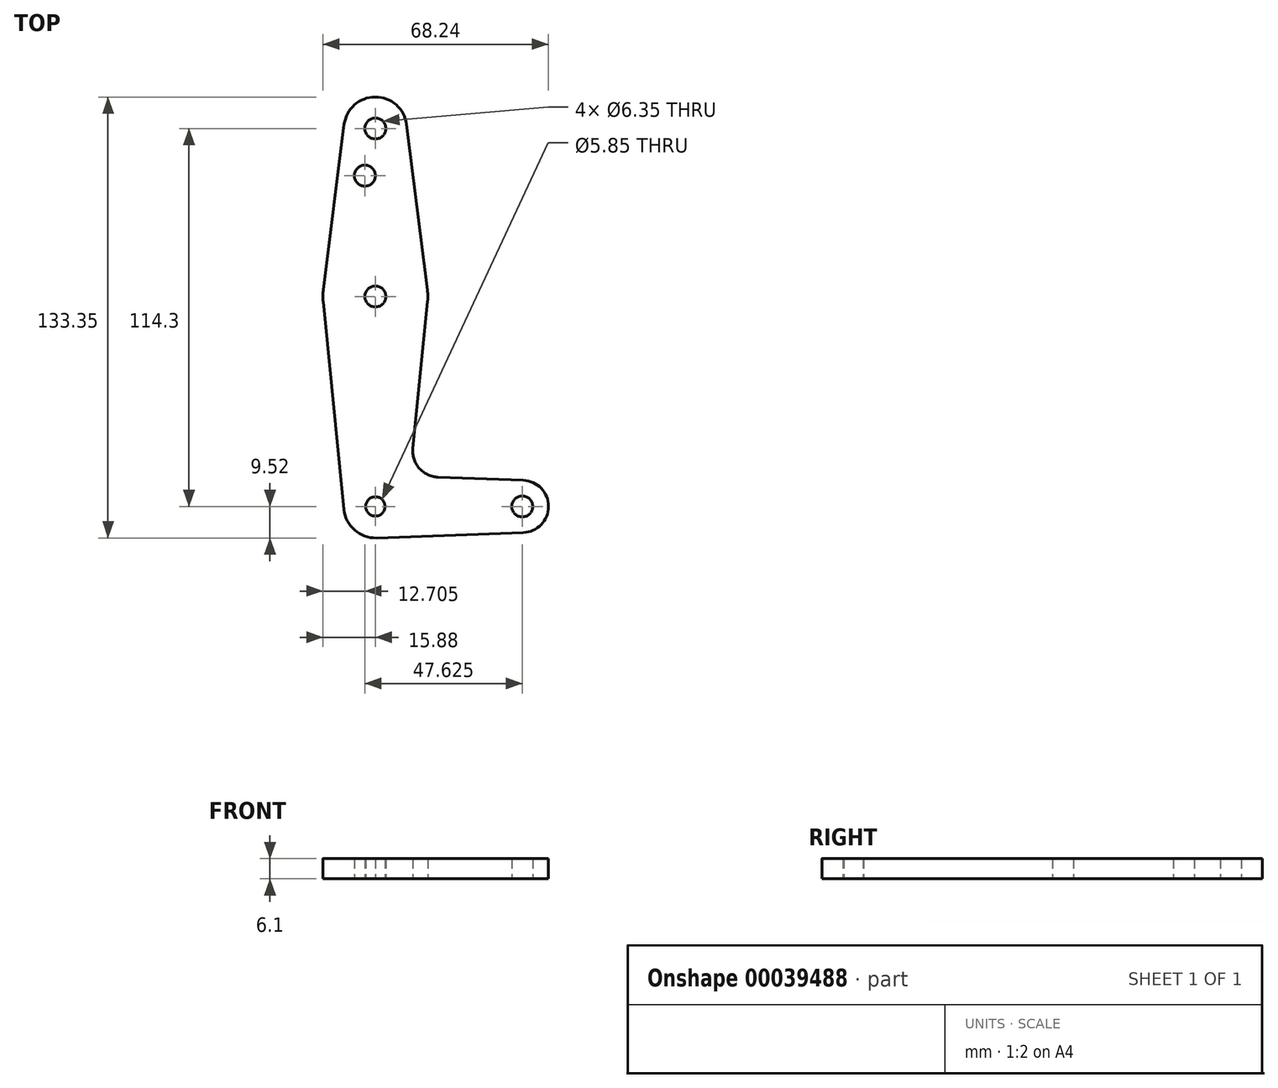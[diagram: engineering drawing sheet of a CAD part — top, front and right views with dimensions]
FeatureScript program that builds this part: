
annotation { "Feature Type Name" : "Feature", "Feature Type Description" : "" }
export const myFeature = defineFeature(function(context is Context, id is Id, definition is map)
    precondition{}
    {
        {
            var Q0;
            Q0=qCreatedBy(makeId("Top.planeOp"),FACE);
            var sketch = newSketch(context, id + "F0", { "sketchPlane" : qUnion([Q0])});
            skLineSegment(sketch, "E0", {"start": v(0, 0) * mm, "end": v(0, 114.3) * mm, "construction": true});
            skLineSegment(sketch, "E1", {"start": v(0, 0) * mm, "end": v(44.45, 0) * mm, "construction": true});
            skCircle(sketch, "E2", {"center": v(44.45, 0) * mm, "radius": 7.91 * mm});
            skCircle(sketch, "E3", {"center": v(0, 114.3) * mm, "radius": 9.53 * mm});
            skCircle(sketch, "E4", {"center": v(0, 0) * mm, "radius": 9.53 * mm});
            skCircle(sketch, "E5", {"center": v(0, 63.5) * mm, "radius": 15.88 * mm});
            skLineSegment(sketch, "E6", {"start": v(-9.45, 115.5) * mm, "end": v(-15.75, 65.48) * mm});
            skLineSegment(sketch, "E7", {"start": v(11.34, 17.58) * mm, "end": v(15.8, 61.91) * mm});
            skLineSegment(sketch, "E8", {"start": v(9.45, 115.5) * mm, "end": v(15.75, 65.48) * mm});
            skLineSegment(sketch, "E9", {"start": v(44.74, 7.9) * mm, "end": v(18.96, 8.84) * mm});
            skLineSegment(sketch, "E10", {"start": v(44.74, -7.9) * mm, "end": v(0, -9.53) * mm});
            skArc(sketch, "E11.filletArc", {"start": v(11.34, 17.58) * mm, "mid": v(13.26, 11.56) * mm, "end": v(18.96, 8.84) * mm});
            skCircle(sketch, "E12", {"center": v(-3.18, 100.03) * mm, "radius": 3.18 * mm});
            skLineSegment(sketch, "E13", {"start": v(-9.48, -0.95) * mm, "end": v(-15.8, 61.91) * mm});
            skCircle(sketch, "E14", {"center": v(44.45, 0) * mm, "radius": 3.18 * mm});
            skCircle(sketch, "E15", {"center": v(0, 0) * mm, "radius": 2.92 * mm});
            skCircle(sketch, "E16", {"center": v(0, 114.3) * mm, "radius": 3.18 * mm});
            skCircle(sketch, "E17", {"center": v(0, 63.5) * mm, "radius": 3.18 * mm});
            skSolve(sketch);
        }
        {
            var Q0;
            Q0 = qSketchRegion(id + "F0", true);
            extrude(context, id + "F1", {"entities" : qUnion([Q0]), "depth" : 3.05 * mm});
        }
        {
            var Q0;
            Q0=makeQuery(id+"F1.opExtrude","CAP_FACE",FACE,{"disambiguationData":[OSD([sQuery(id+"F0.wireOp",EDGE,"E2"),sQuery(id+"F0.wireOp",EDGE,"E3"),sQuery(id+"F0.wireOp",EDGE,"E4"),sQuery(id+"F0.wireOp",EDGE,"E5"),sQuery(id+"F0.wireOp",EDGE,"E6"),sQuery(id+"F0.wireOp",EDGE,"E7"),sQuery(id+"F0.wireOp",EDGE,"E8"),sQuery(id+"F0.wireOp",EDGE,"E9"),sQuery(id+"F0.wireOp",EDGE,"E10"),sQuery(id+"F0.wireOp",EDGE,"E11.filletArc"),sQuery(id+"F0.wireOp",EDGE,"E12"),sQuery(id+"F0.wireOp",EDGE,"E13"),sQuery(id+"F0.wireOp",EDGE,"E14"),sQuery(id+"F0.wireOp",EDGE,"E15"),sQuery(id+"F0.wireOp",EDGE,"E16"),sQuery(id+"F0.wireOp",EDGE,"E17")])],"isStart":false});
            extrude(context, id + "F2", {"entities" : qUnion([Q0]), "operationType" : NewBodyOperationType.ADD, "depth" : 3.05 * mm});
        }
    });
